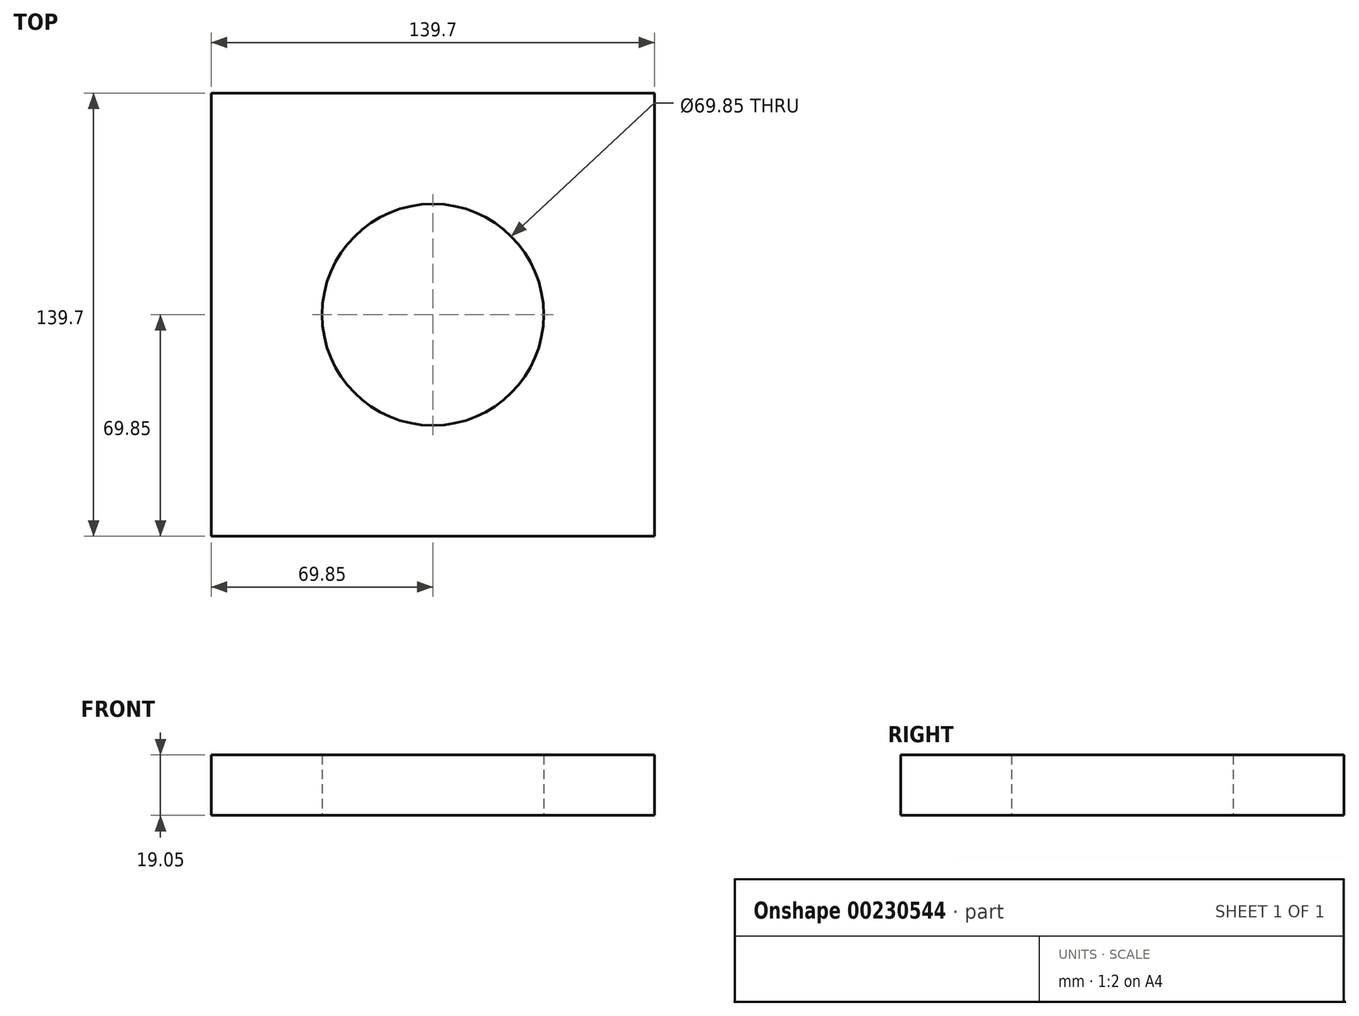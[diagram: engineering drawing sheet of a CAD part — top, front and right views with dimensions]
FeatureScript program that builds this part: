
annotation { "Feature Type Name" : "Feature", "Feature Type Description" : "" }
export const myFeature = defineFeature(function(context is Context, id is Id, definition is map)
    precondition{}
    {
        {
            var Q0;
            Q0=qCreatedBy(makeId("Top.planeOp"),FACE);
            var sketch = newSketch(context, id + "F0", { "sketchPlane" : qUnion([Q0])});
            skLineSegment(sketch, "E0.bottom", {"start": v(-69.85, 69.85) * mm, "end": v(69.85, 69.85) * mm});
            skLineSegment(sketch, "E0.top", {"start": v(-69.85, -69.85) * mm, "end": v(69.85, -69.85) * mm});
            skLineSegment(sketch, "E0.left", {"start": v(-69.85, 69.85) * mm, "end": v(-69.85, -69.85) * mm});
            skLineSegment(sketch, "E0.right", {"start": v(69.85, 69.85) * mm, "end": v(69.85, -69.85) * mm});
            skPoint(sketch, "E0.middle", {"position": v(0, 0) * mm});
            skCircle(sketch, "E1", {"center": v(0, 0) * mm, "radius": 34.93 * mm});
            skSolve(sketch);
        }
        {
            var Q0;
            Q0 = qSketchRegion(id + "F0", true);
            extrude(context, id + "F1", {"entities" : qUnion([Q0]), "depth" : 19.05 * mm});
        }
    });
